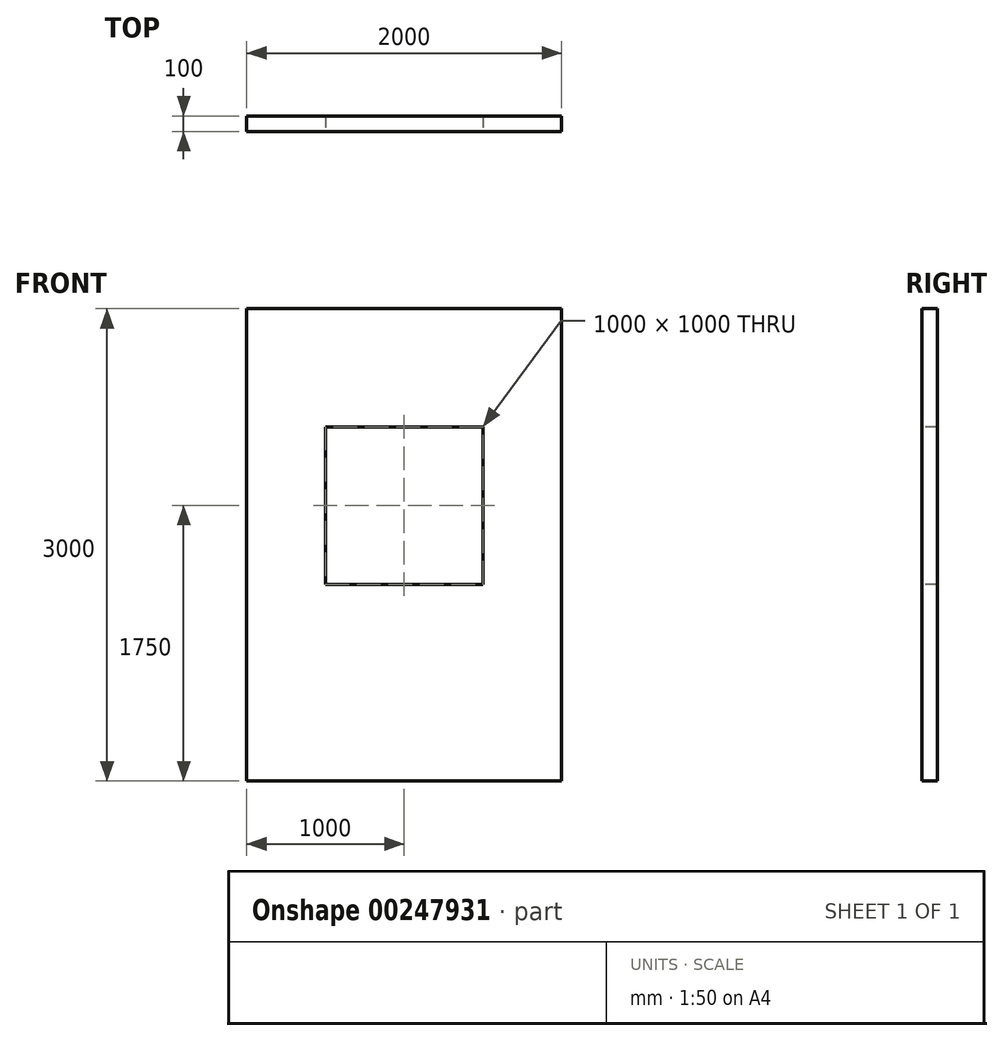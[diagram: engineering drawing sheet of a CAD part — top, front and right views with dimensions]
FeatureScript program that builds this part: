
annotation { "Feature Type Name" : "Feature", "Feature Type Description" : "" }
export const myFeature = defineFeature(function(context is Context, id is Id, definition is map)
    precondition{}
    {
        {
            var Q0;
            Q0=qCreatedBy(makeId("Front.planeOp"),FACE);
            var sketch = newSketch(context, id + "F0", { "sketchPlane" : qUnion([Q0])});
            skLineSegment(sketch, "E0.bottom", {"start": v(1000, 0) * mm, "end": v(-1000, 0) * mm});
            skLineSegment(sketch, "E0.top", {"start": v(1000, 3000) * mm, "end": v(-1000, 3000) * mm});
            skLineSegment(sketch, "E0.left", {"start": v(1000, 0) * mm, "end": v(1000, 3000) * mm});
            skLineSegment(sketch, "E0.right", {"start": v(-1000, 0) * mm, "end": v(-1000, 3000) * mm});
            skPoint(sketch, "E0.middle", {"position": v(0, 1500) * mm});
            skSolve(sketch);
        }
        {
            var Q0;
            Q0=makeQuery(id+"F0.imprint","IMPRINT",FACE,{"disambiguationData":[TD([[makeQuery(id+"F0.imprint","IMPRINT",EDGE,{"derivedFrom":sQuery(id+"F0.wireOp",EDGE,"E0.bottom")}),-1.0]])]});
            extrude(context, id + "F1", {"entities" : qUnion([Q0]), "endBound" : BoundingType.SYMMETRIC, "depth" : 100 * mm});
        }
        {
            var Q0;
            Q0=makeQuery(id+"F1.opExtrude","CAP_FACE",FACE,{"disambiguationData":[OSD([sQuery(id+"F0.wireOp",EDGE,"E0.bottom"),sQuery(id+"F0.wireOp",EDGE,"E0.top"),sQuery(id+"F0.wireOp",EDGE,"E0.left"),sQuery(id+"F0.wireOp",EDGE,"E0.right")])],"isStart":false});
            var sketch = newSketch(context, id + "F2", { "sketchPlane" : qUnion([Q0])});
            skLineSegment(sketch, "E1.bottom", {"start": v(500, 1250) * mm, "end": v(-500, 1250) * mm});
            skLineSegment(sketch, "E1.top", {"start": v(500, 2250) * mm, "end": v(-500, 2250) * mm});
            skLineSegment(sketch, "E1.left", {"start": v(500, 1250) * mm, "end": v(500, 2250) * mm});
            skLineSegment(sketch, "E1.right", {"start": v(-500, 1250) * mm, "end": v(-500, 2250) * mm});
            skPoint(sketch, "E1.middle", {"position": v(0, 1750) * mm});
            skSolve(sketch);
        }
        {
            var Q0;
            Q0=makeQuery(id+"F2.imprint","IMPRINT",FACE,{"disambiguationData":[TD([[makeQuery(id+"F2.imprint","IMPRINT",EDGE,{"derivedFrom":sQuery(id+"F2.wireOp",EDGE,"IdCekE0X-Srk5-c7yG-rf7o-qwZRKCNb5MFu.bottom")}),-1.0]])]});
            var Q1;
            Q1=makeQuery(id+"F2.imprint","IMPRINT",FACE,{"disambiguationData":[TD([[makeQuery(id+"F2.imprint","IMPRINT",EDGE,{"derivedFrom":sQuery(id+"F2.wireOp",EDGE,"E1.bottom")}),-1.0]])]});
            extrude(context, id + "F3", {"entities" : qUnion([Q0, Q1]), "operationType" : NewBodyOperationType.REMOVE, "endBound" : BoundingType.THROUGH_ALL, "oppositeDirection" : true, "depth" : 25 * mm});
        }
    });
